# Revit family: Indirect-Water-Heater_AO_Smith-IT-300_F_B
name_source: partatom
category: Mechanical Equipment
revit_build: Autodesk Revit 2016 (Build: 20170117_1200(x64)
units: mm (PartAtom-declared; Revit-internal decimal feet)

## family parameters
Always vertical = Yes
Cut with Voids When Loaded = No
OmniClass Number = 23.75.00.00
OmniClass Title = Climate Control (HVAC)
Part Type = Normal
Room Calculation Point = No
Round Connector Dimension = Use Radius
Shared = No
Work Plane-Based = No

## types (1)
- Indirect-Water-Heater_AO_Smith-IT-300_F_B
    1er Entretien (check-up) = 3 mois après l'installation
    2ème Entretien (Entretien Général) = 12 mois après l'installation
    Assembly Code = D3010
    BIM Content Developer = CAD & Company
    BIM Content Developer URL = http://www.cadcompany.nl
    Capacité - Cuve = 300 m³
    Capacité - Échangeur Inférieur = 8.9 m³
    Charge Maximale au Sol = 425.00 kg
    Description = Cuve Indirects Fournis d’un Échangeur
    Destination / Pays = France
    Diamètre (avec Isolation) = 750 mm  [stored 2.46063 ft]
    Diamètre (sans Isolation) = 550 mm  [stored 1.80446 ft]
    Débit de vidage en Continu à ΔT = 28°C = 1413
    Débit de vidage en Continu à ΔT = 44°C = 899
    Débit de vidage en Continu à ΔT = 50°C = 791
    Débit de vidage en Continu à ΔT = 55°C = 719
    Débit de vidage en Continu à ΔT = 70°C = 565
    Débit de vidage à ΔT = 28°C après 120 min. = 3347.0 L
    Débit de vidage à ΔT = 28°C après 30 min. = 1228.0 L
    Débit de vidage à ΔT = 28°C après 60 min. = 1934.0 L
    Débit de vidage à ΔT = 28°C après 90 min. = 2641.0 L
    Débit de vidage à ΔT = 44°C après 120 min. = 2130.0 L
    Débit de vidage à ΔT = 44°C après 30 min. = 781.0 L
    Débit de vidage à ΔT = 44°C après 60 min. = 1231.0 L
    Débit de vidage à ΔT = 44°C après 90 min. = 1680.0 L
    Débit de vidage à ΔT = 50°C après 120 min. = 1874.0 L
    Débit de vidage à ΔT = 50°C après 30 min. = 688.0 L
    Débit de vidage à ΔT = 50°C après 60 min. = 1083.0 L
    Débit de vidage à ΔT = 50°C après 90 min. = 1479.0 L
    Débit de vidage à ΔT = 55°C après 120 min. = 1704.0 L
    Débit de vidage à ΔT = 55°C après 30 min. = 625.0 L
    Débit de vidage à ΔT = 55°C après 60 min. = 985.0 L
    Débit de vidage à ΔT = 55°C après 90 min. = 1344.0 L
    Débit de vidage à ΔT = 70°C après 120 min. = 1339.0 L
    Débit de vidage à ΔT = 70°C après 30 min. = 491.0 L
    Débit de vidage à ΔT = 70°C après 60 min. = 774.0 L
    Débit de vidage à ΔT = 70°C après 90 min. = 1056.0 L
    Débit à 80ºC/60ºC - Échangeur Inférieur = 1978
    Epaisseur d'Isolation = 100 mm  [stored 0.328084 ft]
    Fabricant No. = E 7110
    Garantie Pièces = 12 mois
    Garantie sur la Cuve = 36 mois
    Guide de Produit = https://www.aosmithinternational.com
    Hauteur (avec Isolation) = 1650 mm  [stored 5.41339 ft]
    Hauteur (sans Isolation) = 1545 mm  [stored 5.0689 ft]
    Hauteur d'Emballage = 1770 mm  [stored 5.80709 ft]
    Hauteur de l'Alimentation en eau Froide = 110 mm  [stored 0.360892 ft]
    Hauteur de la Sortie d'eau Chaude = 1460 mm  [stored 4.79003 ft]
    Largeur d'Emballage = 800 mm  [stored 2.62467 ft]
    Manufacturer = A.O. Smith Water Products Company b.v.
    Max. Température de l'eau - Réservoir = 95 °C
    Model = IT 300 F B
    Nombre de modèle du produit (EAN) = 8717449181758
    Perte de Pression à 80ºC/60ºC - Échangeur Inférieur = 5600.0 Pa
    Pertes en Veille = 0 W
    Pertes en Veille - tous les jours (24h) = 0
    Poids de Transport = 133.00 kg
    Poids à vide = 125.00 kg
    Pression de Service Maximale - Réservoir = 1000000.0 Pa
    Pression de Service Maximale - Échangeur Inférieur = 1600000.0 Pa
    Production Nominale - Échangeur Inférieur = 46000 W
    Profondeur d'Emballage = 800 mm  [stored 2.62467 ft]
    Raccord d'Alimentation en Eau Froide = 1"
    Raccord de Sortie d'Eau Chaude = 1"
    Raccord de la Soupape de Vidange = 1"
    Spécifications du Produit = https://www.aosmithinternational.com
    Surface d'Échange de Chaleur - Échangeur Inférieur = 1.47 m²
    Temps de réchauffement à ΔT = 28°C = 13
    Temps de réchauffement à ΔT = 44°C = 20
    Temps de réchauffement à ΔT = 50°C = 22
    Temps de réchauffement à ΔT = 55°C = 25
    Temps de réchauffement à ΔT = 70°C = 31
    Température Maximale - Échangeur Inférieur = 110 °C
    Type d'Emballage = Plastique et Bois
    URL = http://www.aosmith.fr
    Workspace Diameter = 1750 mm  [stored 5.74147 ft]
    Workspace Height = 2650 mm  [stored 8.69423 ft]
    espace de travail = 860 mm
    l'Intervalle d'Entretien = 12 mois

note: [stored X ft] marks values corroborated as IEEE doubles in the binary element streams (Revit-internal decimal feet)

## geometry (parser evidence)
native form markers: Blend x2, Sweep x22
no freeform markers — native parametric forms only
